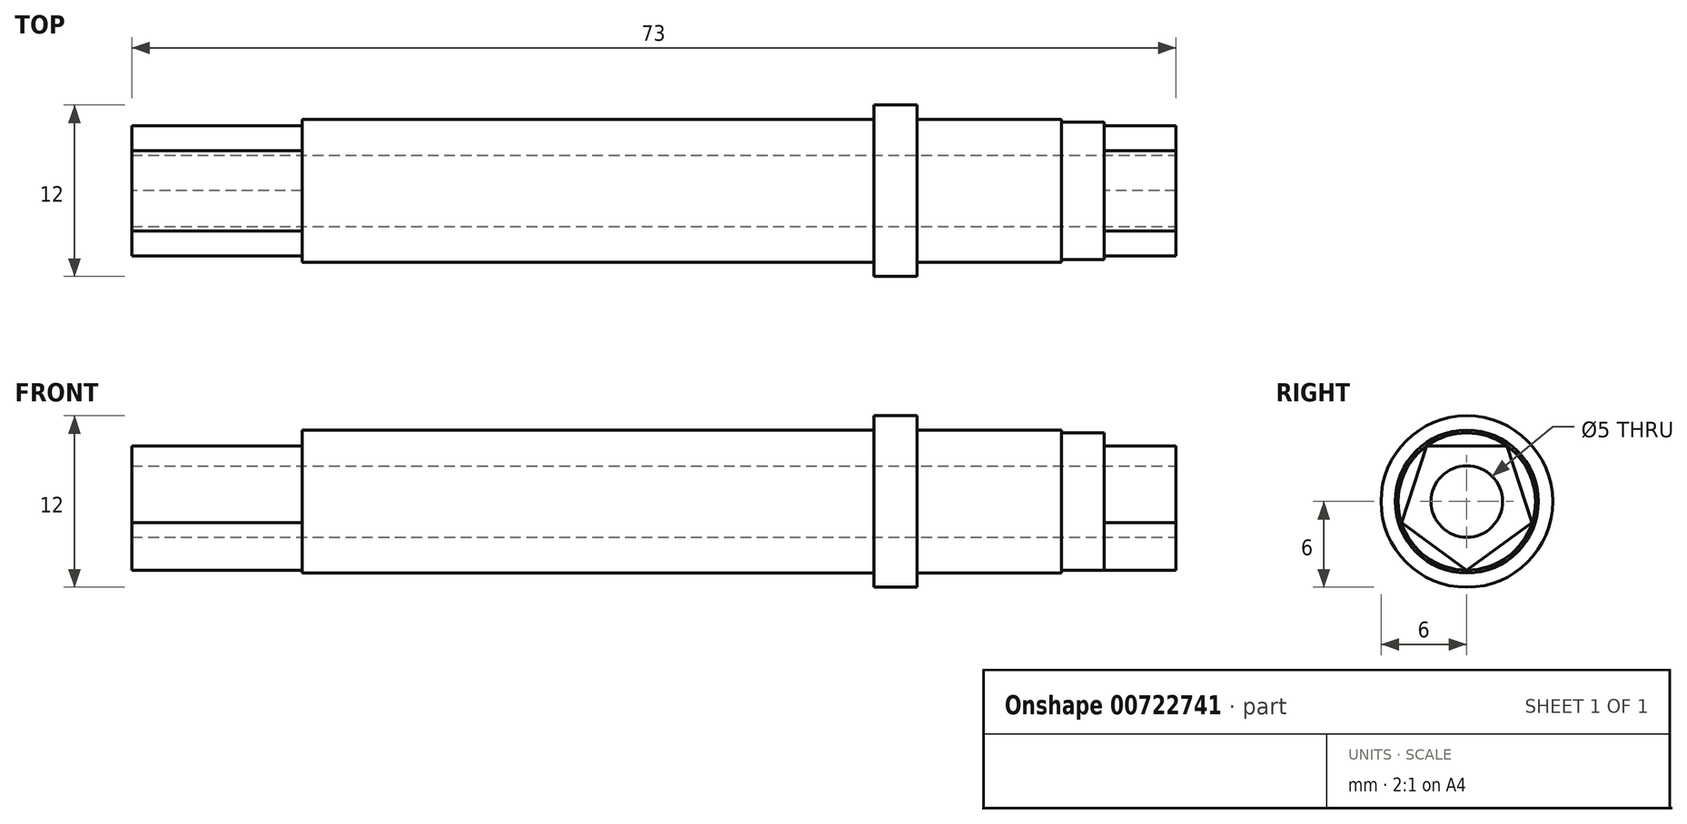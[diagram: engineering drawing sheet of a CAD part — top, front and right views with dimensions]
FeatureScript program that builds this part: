
annotation { "Feature Type Name" : "Feature", "Feature Type Description" : "" }
export const myFeature = defineFeature(function(context is Context, id is Id, definition is map)
    precondition{}
    {
        {
            var Q0;
            Q0=qCreatedBy(makeId("Right.planeOp"),FACE);
            var sketch = newSketch(context, id + "F0", { "sketchPlane" : qUnion([Q0])});
            skCircle(sketch, "E0", {"center": v(0, 0) * mm, "radius": 5 * mm});
            skSolve(sketch);
        }
        {
            var Q0;
            Q0=qSketchRegion(id+"F0",true);
            extrude(context, id + "F1", {"entities" : qUnion([Q0]), "oppositeDirection" : true, "depth" : 10.1 * mm, "offsetDistance" : 25 * mm});
        }
        {
            var Q0;
            Q0=makeQuery(id+"F1.opExtrude","CAP_FACE",FACE,{"disambiguationData":[OSD([sQuery(id+"F0.wireOp",EDGE,"E0")])],"isStart":true});
            var sketch = newSketch(context, id + "F2", { "sketchPlane" : qUnion([Q0])});
            skCircle(sketch, "E1", {"center": v(0, 0) * mm, "radius": 4.8 * mm});
            skSolve(sketch);
        }
        {
            var Q0;
            Q0=qSketchRegion(id+"F2",true);
            extrude(context, id + "F3", {"entities" : qUnion([Q0]), "operationType" : NewBodyOperationType.ADD, "depth" : 3 * mm, "offsetDistance" : 25 * mm});
        }
        {
            var Q0;
            Q0=makeQuery(id+"F3.opExtrude","CAP_FACE",FACE,{"disambiguationData":[OSD([sQuery(id+"F2.wireOp",EDGE,"E1")])],"isStart":false});
            var sketch = newSketch(context, id + "F4", { "sketchPlane" : qUnion([Q0])});
            skCircle(sketch, "E2.cCircle", {"center": v(0, 0) * mm, "radius": 4.8 * mm, "construction": true});
            skLineSegment(sketch, "E2.0", {"start": v(0, -4.8) * mm, "end": v(-4.57, -1.48) * mm});
            skLineSegment(sketch, "E2.1", {"start": v(-4.57, -1.48) * mm, "end": v(-2.82, 3.88) * mm});
            skLineSegment(sketch, "E2.2", {"start": v(-2.82, 3.88) * mm, "end": v(2.82, 3.88) * mm});
            skLineSegment(sketch, "E2.3", {"start": v(2.82, 3.88) * mm, "end": v(4.57, -1.48) * mm});
            skLineSegment(sketch, "E2.4", {"start": v(4.57, -1.48) * mm, "end": v(0, -4.8) * mm});
            skSolve(sketch);
        }
        {
            var Q0;
            Q0=qSketchRegion(id+"F4",true);
            extrude(context, id + "F5", {"entities" : qUnion([Q0]), "operationType" : NewBodyOperationType.ADD, "depth" : 5 * mm, "offsetDistance" : 25 * mm, "hasSecondDirection" : true, "secondDirectionOppositeDirection" : true, "secondDirectionDepth" : 68 * mm});
        }
        {
            var Q0;
            Q0=makeQuery(id+"F1.opExtrude","CAP_FACE",FACE,{"disambiguationData":[OSD([sQuery(id+"F0.wireOp",EDGE,"E0")])],"isStart":false});
            var sketch = newSketch(context, id + "F6", { "sketchPlane" : qUnion([Q0])});
            skCircle(sketch, "E3", {"center": v(0, 0) * mm, "radius": 6 * mm});
            skSolve(sketch);
        }
        {
            var Q0;
            Q0 = qSketchRegion(id + "F6", true);
            extrude(context, id + "F7", {"entities" : qUnion([Q0]), "operationType" : NewBodyOperationType.ADD, "depth" : 3 * mm, "offsetDistance" : 25 * mm});
        }
        {
            var Q0;
            {var subQ0=sQuery(id+"F6.wireOp",EDGE,"E3");Q0=makeQuery(id+"F7.boolean.opBoolean","SPLIT",FACE,{"disambiguationData":[TD([makeQuery(id+"F5.opExtrude","SWEPT_FACE",FACE,{"disambiguationData":[OSD([sQuery(id+"F4.wireOp",EDGE,"E2.0")])]})])],"derivedFrom":makeQuery(id+"F7.opExtrude","CAP_FACE",FACE,{"disambiguationData":[OSD([subQ0])],"isStart":false})});}
            var sketch = newSketch(context, id + "F8", { "sketchPlane" : qUnion([Q0])});
            skCircle(sketch, "E4", {"center": v(0, 0) * mm, "radius": 5 * mm});
            skSolve(sketch);
        }
        {
            var Q0;
            Q0 = qSketchRegion(id + "F8", true);
            extrude(context, id + "F9", {"entities" : qUnion([Q0]), "operationType" : NewBodyOperationType.ADD, "depth" : 40 * mm, "offsetDistance" : 25 * mm});
        }
        {
            var Q0;
            Q0=makeQuery(id+"F5.opExtrude","CAP_FACE",FACE,{"disambiguationData":[OSD([sQuery(id+"F4.wireOp",EDGE,"E2.0"),sQuery(id+"F4.wireOp",EDGE,"E2.1"),sQuery(id+"F4.wireOp",EDGE,"E2.2"),sQuery(id+"F4.wireOp",EDGE,"E2.3"),sQuery(id+"F4.wireOp",EDGE,"E2.4")])],"isStart":false});
            var sketch = newSketch(context, id + "F10", { "sketchPlane" : qUnion([Q0])});
            skCircle(sketch, "E5", {"center": v(0, 0) * mm, "radius": 2.5 * mm});
            skSolve(sketch);
        }
        {
            var Q0;
            Q0 = qSketchRegion(id + "F10", true);
            extrude(context, id + "F11", {"entities" : qUnion([Q0]), "operationType" : NewBodyOperationType.REMOVE, "oppositeDirection" : true, "depth" : 80 * mm, "offsetDistance" : 25 * mm});
        }
    });
